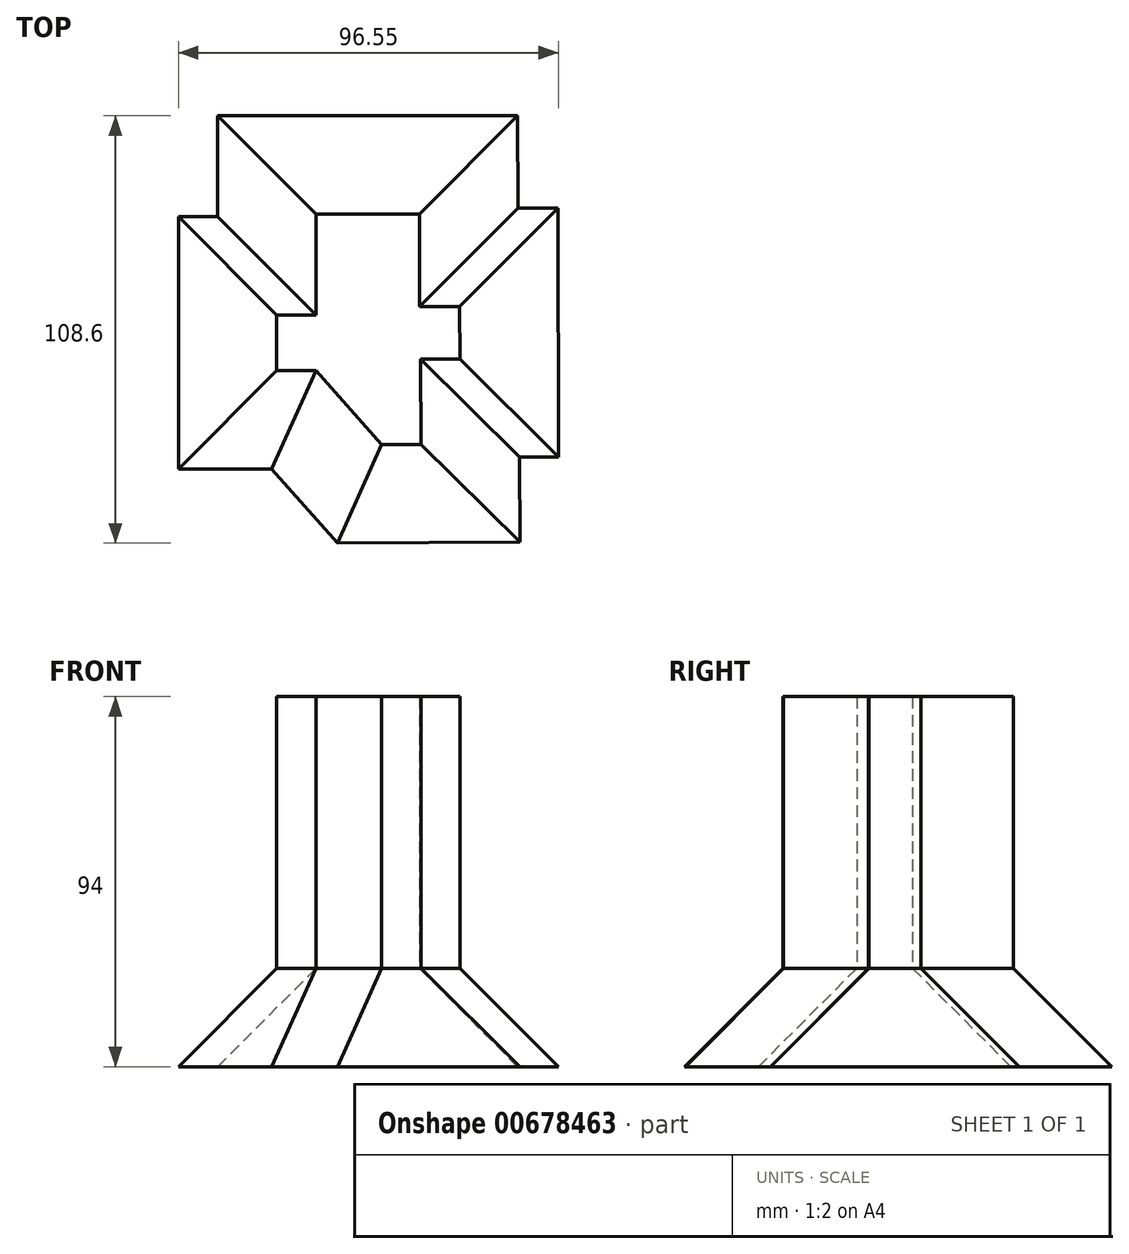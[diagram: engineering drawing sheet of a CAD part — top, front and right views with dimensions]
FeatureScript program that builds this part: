
annotation { "Feature Type Name" : "Feature", "Feature Type Description" : "" }
export const myFeature = defineFeature(function(context is Context, id is Id, definition is map)
    precondition{}
    {
        {
            var Q0;
            Q0=qCreatedBy(makeId("Front.planeOp"),FACE);
            var sketch = newSketch(context, id + "F0", { "sketchPlane" : qUnion([Q0])});
            skLineSegment(sketch, "E0", {"start": v(-25.24, 0) * mm, "end": v(-4.1, -27.35) * mm});
            skLineSegment(sketch, "E1", {"start": v(-4.1, -27.35) * mm, "end": v(10.97, -27.35) * mm});
            skLineSegment(sketch, "E2", {"start": v(10.97, -27.35) * mm, "end": v(10.97, 0) * mm});
            skLineSegment(sketch, "E3", {"start": v(10.97, 0) * mm, "end": v(20.22, 0) * mm});
            skLineSegment(sketch, "E4", {"start": v(20.22, 0) * mm, "end": v(20.22, 10.7) * mm});
            skLineSegment(sketch, "E5", {"start": v(20.22, 10.7) * mm, "end": v(11.23, 10.7) * mm});
            skLineSegment(sketch, "E6", {"start": v(11.23, 10.7) * mm, "end": v(11.5, 24.44) * mm});
            skLineSegment(sketch, "E7", {"start": v(11.5, 24.44) * mm, "end": v(-26.55, 25.18) * mm});
            skLineSegment(sketch, "E8", {"start": v(-26.55, 25.18) * mm, "end": v(-26.55, 12.02) * mm});
            skLineSegment(sketch, "E9", {"start": v(-26.55, 12.02) * mm, "end": v(-37.92, 12.02) * mm});
            skLineSegment(sketch, "E10", {"start": v(-37.92, 12.02) * mm, "end": v(-37.92, 0) * mm});
            skLineSegment(sketch, "E11", {"start": v(-37.92, 0) * mm, "end": v(-25.24, 0) * mm});
            skSolve(sketch);
        }
        {
            var Q0;
            Q0 = qSketchRegion(id + "F0", true);
            extrude(context, id + "F1", {"entities" : qUnion([Q0]), "depth" : 25 * mm, "offsetDistance" : 25 * mm});
        }
        {
            var Q0;
            Q0=makeQuery(id+"F1.opExtrude","SWEPT_BODY",BODY,{"disambiguationData":[OSD([sQuery(id+"F0.wireOp",EDGE,"E0"),sQuery(id+"F0.wireOp",EDGE,"E1"),sQuery(id+"F0.wireOp",EDGE,"E2"),sQuery(id+"F0.wireOp",EDGE,"E3"),sQuery(id+"F0.wireOp",EDGE,"E4"),sQuery(id+"F0.wireOp",EDGE,"E5"),sQuery(id+"F0.wireOp",EDGE,"E6"),sQuery(id+"F0.wireOp",EDGE,"E7"),sQuery(id+"F0.wireOp",EDGE,"E8"),sQuery(id+"F0.wireOp",EDGE,"E9"),sQuery(id+"F0.wireOp",EDGE,"E10"),sQuery(id+"F0.wireOp",EDGE,"E11")])]});
            deleteBodies(context, id + "F2", {"entities" : qUnion([Q0])});
        }
        {
            var Q0;
            Q0=qCreatedBy(makeId("Top.planeOp"),FACE);
            var sketch = newSketch(context, id + "F3", { "sketchPlane" : qUnion([Q0])});
            skLineSegment(sketch, "E12", {"start": v(-14.6, -9.08) * mm, "end": v(-24.6, -9.08) * mm});
            skLineSegment(sketch, "E13", {"start": v(-24.6, -9.08) * mm, "end": v(-24.6, 5.07) * mm});
            skLineSegment(sketch, "E14", {"start": v(-24.6, 5.07) * mm, "end": v(-14.6, 5.07) * mm});
            skLineSegment(sketch, "E15", {"start": v(-14.6, 5.07) * mm, "end": v(-14.6, 30.7) * mm});
            skLineSegment(sketch, "E16", {"start": v(-14.6, 30.7) * mm, "end": v(11.63, 30.7) * mm});
            skLineSegment(sketch, "E17", {"start": v(11.63, 30.7) * mm, "end": v(11.69, 7.19) * mm});
            skLineSegment(sketch, "E18", {"start": v(11.69, 7.19) * mm, "end": v(21.86, 7.21) * mm});
            skLineSegment(sketch, "E19", {"start": v(21.86, 7.21) * mm, "end": v(21.9, -6.07) * mm});
            skLineSegment(sketch, "E20", {"start": v(21.9, -6.07) * mm, "end": v(11.9, -6.09) * mm});
            skLineSegment(sketch, "E21", {"start": v(11.9, -6.09) * mm, "end": v(12, -27.79) * mm});
            skLineSegment(sketch, "E22", {"start": v(12, -27.79) * mm, "end": v(2, -27.84) * mm});
            skLineSegment(sketch, "E23", {"start": v(2, -27.84) * mm, "end": v(-14.6, -9.08) * mm});
            skSolve(sketch);
        }
        {
            var Q0;
            Q0=makeQuery(id+"F3.imprint","IMPRINT",FACE,{"disambiguationData":[TD([[makeQuery(id+"F3.imprint","IMPRINT",EDGE,{"derivedFrom":sQuery(id+"F3.wireOp",EDGE,"E12")}),-1.0]])]});
            extrude(context, id + "F4", {"entities" : qUnion([Q0]), "depth" : 69 * mm, "offsetDistance" : 25 * mm});
        }
        {
            var Q0;
            Q0=makeQuery(id+"F4.opExtrude","CAP_FACE",FACE,{"disambiguationData":[OSD([sQuery(id+"F3.wireOp",EDGE,"E12"),sQuery(id+"F3.wireOp",EDGE,"E13"),sQuery(id+"F3.wireOp",EDGE,"E14"),sQuery(id+"F3.wireOp",EDGE,"E15"),sQuery(id+"F3.wireOp",EDGE,"E16"),sQuery(id+"F3.wireOp",EDGE,"E17"),sQuery(id+"F3.wireOp",EDGE,"E18"),sQuery(id+"F3.wireOp",EDGE,"E19"),sQuery(id+"F3.wireOp",EDGE,"E20"),sQuery(id+"F3.wireOp",EDGE,"E21"),sQuery(id+"F3.wireOp",EDGE,"E22"),sQuery(id+"F3.wireOp",EDGE,"E23")])],"isStart":true});
            extrude(context, id + "F5", {"entities" : qUnion([Q0]), "operationType" : NewBodyOperationType.ADD, "depth" : 25 * mm, "offsetDistance" : 25 * mm, "hasDraft" : true, "draftAngle" : 45 * degree});
        }
    });
